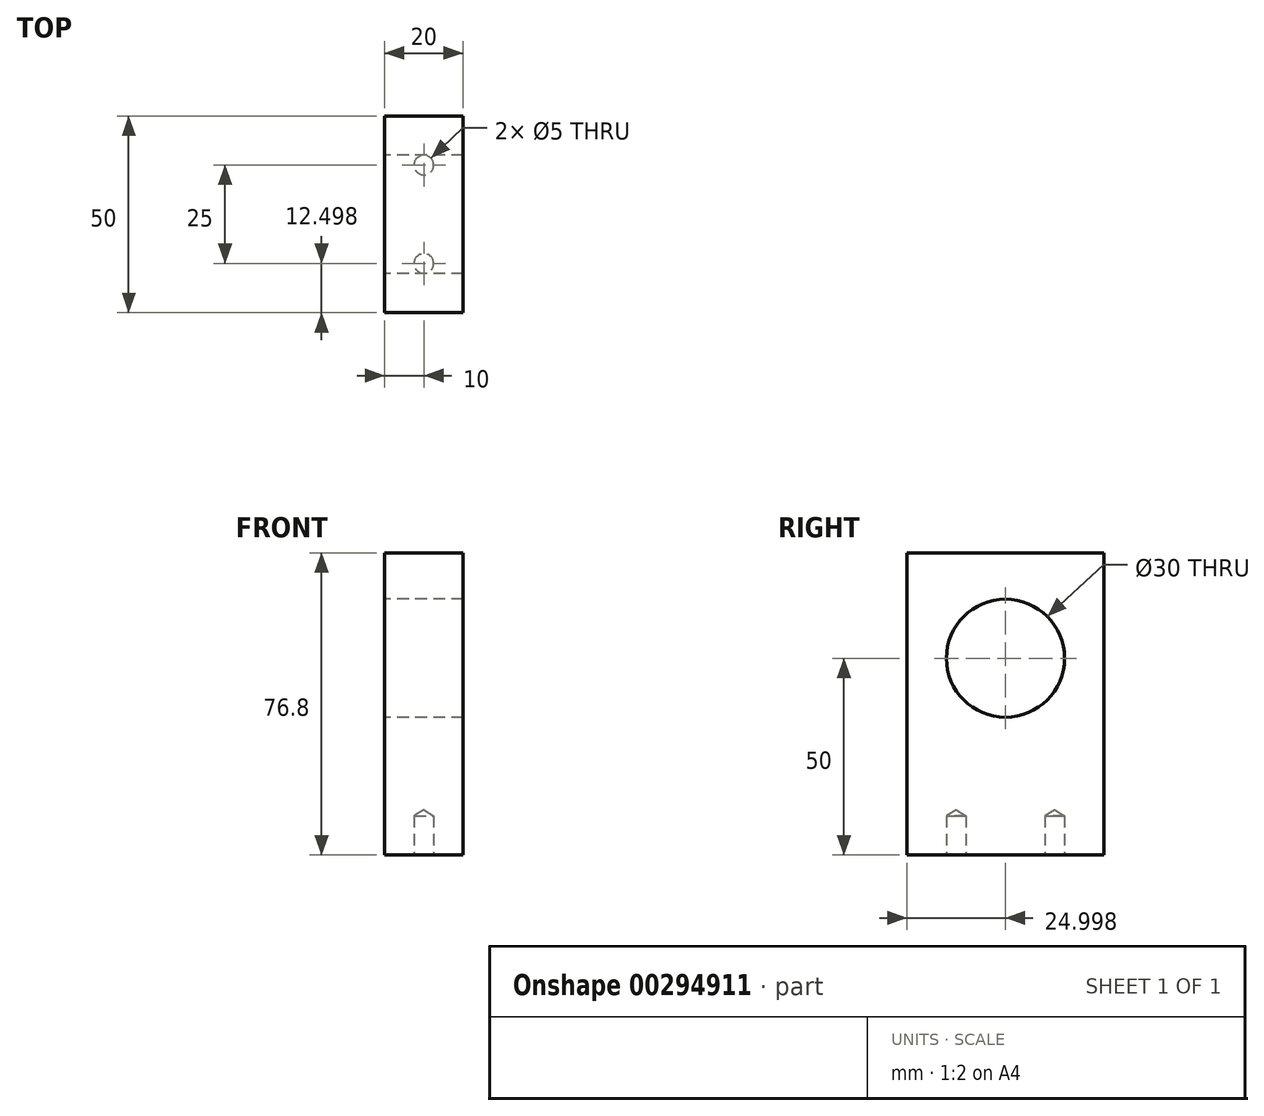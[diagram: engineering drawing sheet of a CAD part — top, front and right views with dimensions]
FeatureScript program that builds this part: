
annotation { "Feature Type Name" : "Feature", "Feature Type Description" : "" }
export const myFeature = defineFeature(function(context is Context, id is Id, definition is map)
    precondition{}
    {
        {
            var Q0;
            Q0=qCreatedBy(makeId("Right.planeOp"),FACE);
            var sketch = newSketch(context, id + "F0", { "sketchPlane" : qUnion([Q0])});
            skLineSegment(sketch, "E0.bottom", {"start": v(13.93, 12.66) * mm, "end": v(63.93, 12.66) * mm});
            skLineSegment(sketch, "E0.top", {"start": v(13.93, 62.66) * mm, "end": v(63.93, 62.66) * mm});
            skLineSegment(sketch, "E0.left", {"start": v(13.93, 12.66) * mm, "end": v(13.93, 62.66) * mm});
            skLineSegment(sketch, "E0.right", {"start": v(63.93, 12.66) * mm, "end": v(63.93, 62.66) * mm});
            skCircle(sketch, "E1", {"center": v(38.93, 62.66) * mm, "radius": 15 * mm});
            skLineSegment(sketch, "E2", {"start": v(13.93, 62.66) * mm, "end": v(13.93, 89.46) * mm});
            skLineSegment(sketch, "E3", {"start": v(13.93, 89.46) * mm, "end": v(63.93, 89.46) * mm});
            skLineSegment(sketch, "E4", {"start": v(63.93, 89.46) * mm, "end": v(63.93, 62.66) * mm});
            skSolve(sketch);
        }
        {
            var Q0;
            Q0=makeQuery(id+"F0.imprint","IMPRINT",FACE,{"disambiguationData":[TD([[makeQuery(id+"F0.imprint","IMPRINT",EDGE,{"derivedFrom":sQuery(id+"F0.wireOp",EDGE,"E0.bottom")}),1.0]])]});
            var Q1;
            {var subQ0=sQuery(id+"F0.wireOp",EDGE,"E2");Q1=makeQuery(id+"F0.imprint","IMPRINT",FACE,{"disambiguationData":[TD([[makeQuery(id+"F0.imprint","IMPRINT",EDGE,{"derivedFrom":subQ0}),-1.0]])]});}
            extrude(context, id + "F1", {"entities" : qUnion([Q0, Q1]), "depth" : 20 * mm, "offsetDistance" : 25 * mm});
        }
        {
            var Q0;
            Q0=makeQuery(id+"F1.opExtrude","SWEPT_FACE",FACE,{"disambiguationData":[OSD([sQuery(id+"F0.wireOp",EDGE,"E0.bottom")])]});
            var sketch = newSketch(context, id + "F2", { "sketchPlane" : qUnion([Q0])});
            skLineSegment(sketch, "E5", {"start": v(20, -38.93) * mm, "end": v(0, -38.93) * mm, "construction": true});
            skLineSegment(sketch, "E6", {"start": v(10, -63.93) * mm, "end": v(10, -38.93) * mm, "construction": true});
            skLineSegment(sketch, "E7", {"start": v(10, -38.93) * mm, "end": v(10, -13.93) * mm, "construction": true});
            skPoint(sketch, "E8", {"position": v(10, -51.43) * mm});
            skPoint(sketch, "E9", {"position": v(10, -26.43) * mm});
            skSolve(sketch);
        }
        {
            var Q0;
            Q0=sQuery(id+"F2.wireOp",VERTEX,"E8");
            var Q1;
            Q1=sQuery(id+"F2.wireOp",VERTEX,"E9");
            var Q2;
            Q2=makeQuery(id+"F1.opExtrude","SWEPT_BODY",BODY,{"disambiguationData":[OSD([sQuery(id+"F0.wireOp",EDGE,"E0.bottom"),sQuery(id+"F0.wireOp",EDGE,"E0.top"),sQuery(id+"F0.wireOp",EDGE,"E0.left"),sQuery(id+"F0.wireOp",EDGE,"E0.right"),sQuery(id+"F0.wireOp",EDGE,"E1")])]});
            hole(context, id + "F3", {"style" : HoleStyle.SIMPLE, "endStyle" : HoleEndStyle.BLIND, "holeDiameter" : 5 * mm, "holeDepth" : 10 * mm, "tappedDepth" : 12 * mm, "tapClearance" : 3, "locations" : qUnion([Q0, Q1]), "scope" : qUnion([Q2])});
        }
    });
